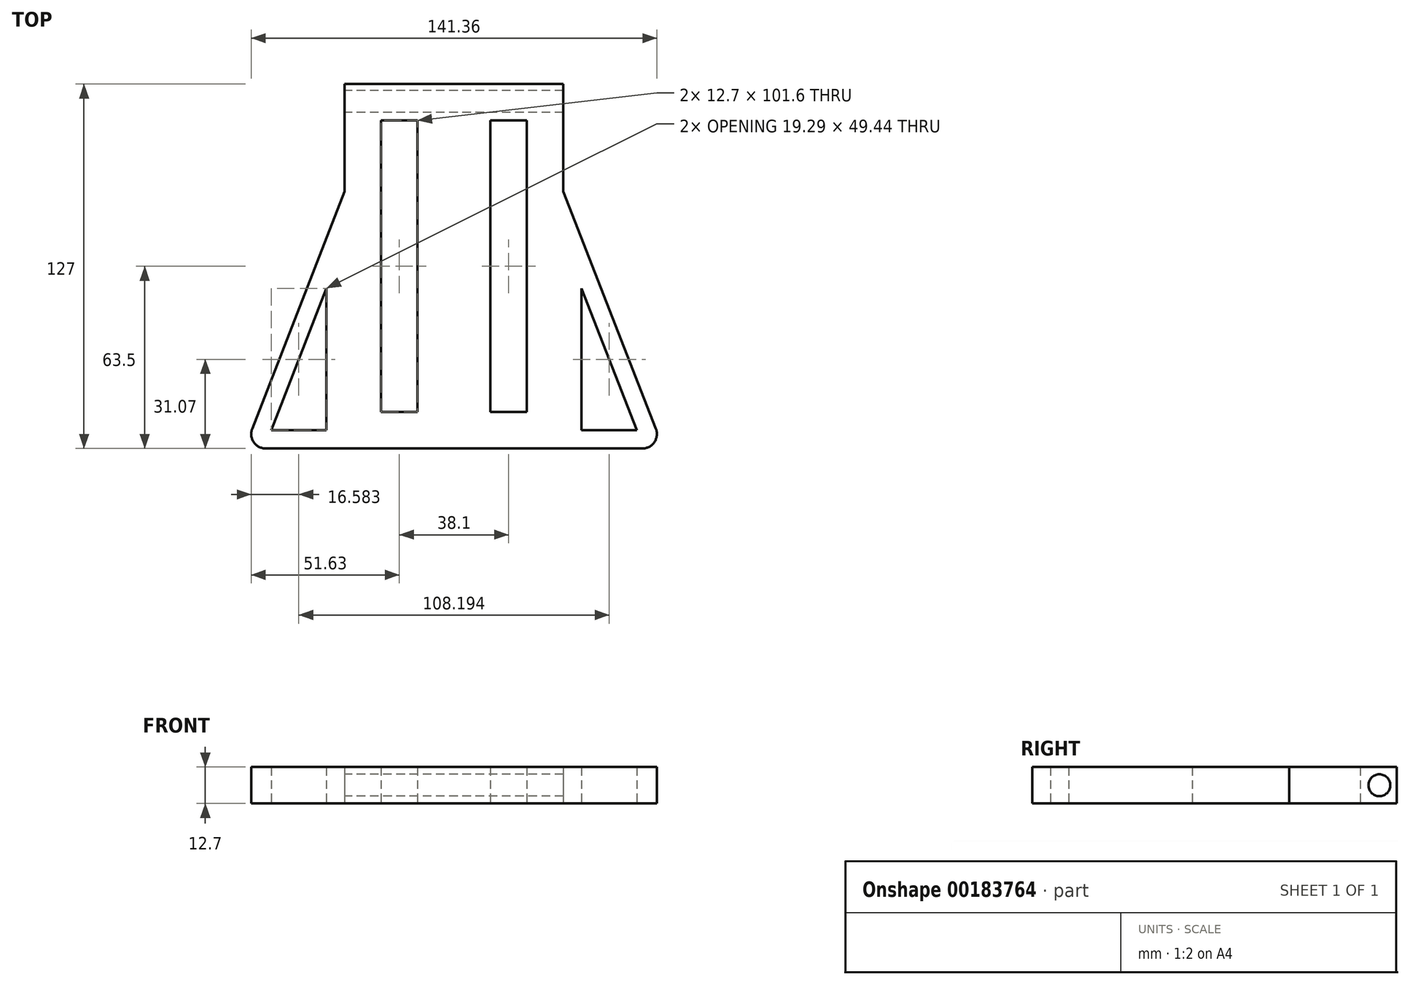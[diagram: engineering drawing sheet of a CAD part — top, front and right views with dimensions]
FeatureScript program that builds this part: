
annotation { "Feature Type Name" : "Feature", "Feature Type Description" : "" }
export const myFeature = defineFeature(function(context is Context, id is Id, definition is map)
    precondition{}
    {
        {
            var Q0;
            Q0=qCreatedBy(makeId("Top.planeOp"),FACE);
            var sketch = newSketch(context, id + "F0", { "sketchPlane" : qUnion([Q0])});
            skLineSegment(sketch, "E0.bottom", {"start": v(38.1, -63.5) * mm, "end": v(-38.1, -63.5) * mm});
            skLineSegment(sketch, "E0.top", {"start": v(38.1, 63.5) * mm, "end": v(-38.1, 63.5) * mm});
            skPoint(sketch, "E0.middle", {"position": v(0, 0) * mm});
            skLineSegment(sketch, "E1", {"start": v(-38.1, 0) * mm, "end": v(38.1, 0) * mm, "construction": true});
            skLineSegment(sketch, "E2", {"start": v(0, 63.5) * mm, "end": v(0, -63.5) * mm, "construction": true});
            skLineSegment(sketch, "E3", {"start": v(-25.4, 50.8) * mm, "end": v(-12.7, 50.8) * mm});
            skLineSegment(sketch, "E4", {"start": v(12.7, 50.8) * mm, "end": v(25.4, 50.8) * mm});
            skLineSegment(sketch, "E5", {"start": v(25.4, -50.8) * mm, "end": v(12.7, -50.8) * mm});
            skLineSegment(sketch, "E6", {"start": v(-12.7, -50.8) * mm, "end": v(-25.4, -50.8) * mm});
            skLineSegment(sketch, "E7", {"start": v(-25.4, 50.8) * mm, "end": v(-25.4, -50.8) * mm});
            skLineSegment(sketch, "E8", {"start": v(-12.7, 50.8) * mm, "end": v(-12.7, -50.8) * mm});
            skLineSegment(sketch, "E9", {"start": v(25.4, 50.8) * mm, "end": v(25.4, -50.8) * mm});
            skLineSegment(sketch, "E10", {"start": v(12.7, 50.8) * mm, "end": v(12.7, -50.8) * mm});
            skLineSegment(sketch, "E11", {"start": v(-38.1, 26.03) * mm, "end": v(-73.04, -63.5) * mm});
            skLineSegment(sketch, "E12", {"start": v(-73.04, -63.5) * mm, "end": v(-38.1, -63.5) * mm});
            skLineSegment(sketch, "E13.MirrorCS", {"start": v(38.1, 26.03) * mm, "end": v(73.04, -63.5) * mm});
            skLineSegment(sketch, "E14.MirrorCS", {"start": v(73.04, -63.5) * mm, "end": v(38.1, -63.5) * mm});
            skLineSegment(sketch, "E15.trimOffspring", {"start": v(-38.1, 26.03) * mm, "end": v(-38.1, 63.5) * mm});
            skLineSegment(sketch, "E16.trimOffspring", {"start": v(38.1, 26.03) * mm, "end": v(38.1, 63.5) * mm});
            skLineSegment(sketch, "E17", {"start": v(-38.1, 26.03) * mm, "end": v(-38.1, -63.5) * mm, "construction": true});
            skLineSegment(sketch, "E18", {"start": v(38.1, 26.03) * mm, "end": v(38.1, -63.5) * mm, "construction": true});
            skLineSegment(sketch, "E19.0", {"start": v(44.45, -7.71) * mm, "end": v(63.74, -57.15) * mm});
            skLineSegment(sketch, "E19.1", {"start": v(44.45, -7.71) * mm, "end": v(44.45, -57.15) * mm});
            skLineSegment(sketch, "E19.2", {"start": v(63.74, -57.15) * mm, "end": v(44.45, -57.15) * mm});
            skLineSegment(sketch, "E20.0", {"start": v(-44.45, -7.71) * mm, "end": v(-63.74, -57.15) * mm});
            skLineSegment(sketch, "E20.1", {"start": v(-44.45, -7.71) * mm, "end": v(-44.45, -57.15) * mm});
            skLineSegment(sketch, "E20.2", {"start": v(-63.74, -57.15) * mm, "end": v(-44.45, -57.15) * mm});
            skSolve(sketch);
        }
        {
            var Q0;
            Q0=makeQuery(id+"F0.imprint","IMPRINT",FACE,{"disambiguationData":[TD([[makeQuery(id+"F0.imprint","IMPRINT",EDGE,{"derivedFrom":sQuery(id+"F0.wireOp",EDGE,"E0.bottom")}),-1.0]])]});
            extrude(context, id + "F1", {"entities" : qUnion([Q0]), "depth" : 12.7 * mm});
        }
        {
            var Q0;
            Q0=makeQuery(id+"F1.opExtrude","SWEPT_EDGE",EDGE,{"disambiguationData":[OSD([sQuery(id+"F0.wireOp",EDGE,"E13.MirrorCS"),sQuery(id+"F0.wireOp",EDGE,"E14.MirrorCS")])]});
            var Q1;
            Q1=makeQuery(id+"F1.opExtrude","SWEPT_EDGE",EDGE,{"disambiguationData":[OSD([sQuery(id+"F0.wireOp",EDGE,"E11"),sQuery(id+"F0.wireOp",EDGE,"E12")])]});
            fillet(context, id + "F2", {"entities" : qUnion([Q0, Q1]), "radius" : 5.08 * mm, "tangentPropagation" : true, "allowEdgeOverflow" : false});
        }
        {
            var Q0;
            Q0=makeQuery(id+"F1.opExtrude","SWEPT_FACE",FACE,{"disambiguationData":[OSD([sQuery(id+"F0.wireOp",EDGE,"E15.trimOffspring")])]});
            var sketch = newSketch(context, id + "F3", { "sketchPlane" : qUnion([Q0])});
            skLineSegment(sketch, "E21", {"start": v(-63.5, 6.35) * mm, "end": v(-26.03, 6.35) * mm, "construction": true});
            skCircle(sketch, "E22", {"center": v(-57.43, 6.35) * mm, "radius": 3.81 * mm});
            skSolve(sketch);
        }
        {
            var Q0;
            Q0 = qSketchRegion(id + "F3", true);
            extrude(context, id + "F4", {"entities" : qUnion([Q0]), "operationType" : NewBodyOperationType.REMOVE, "oppositeDirection" : true, "depth" : 76.2 * mm});
        }
    });
